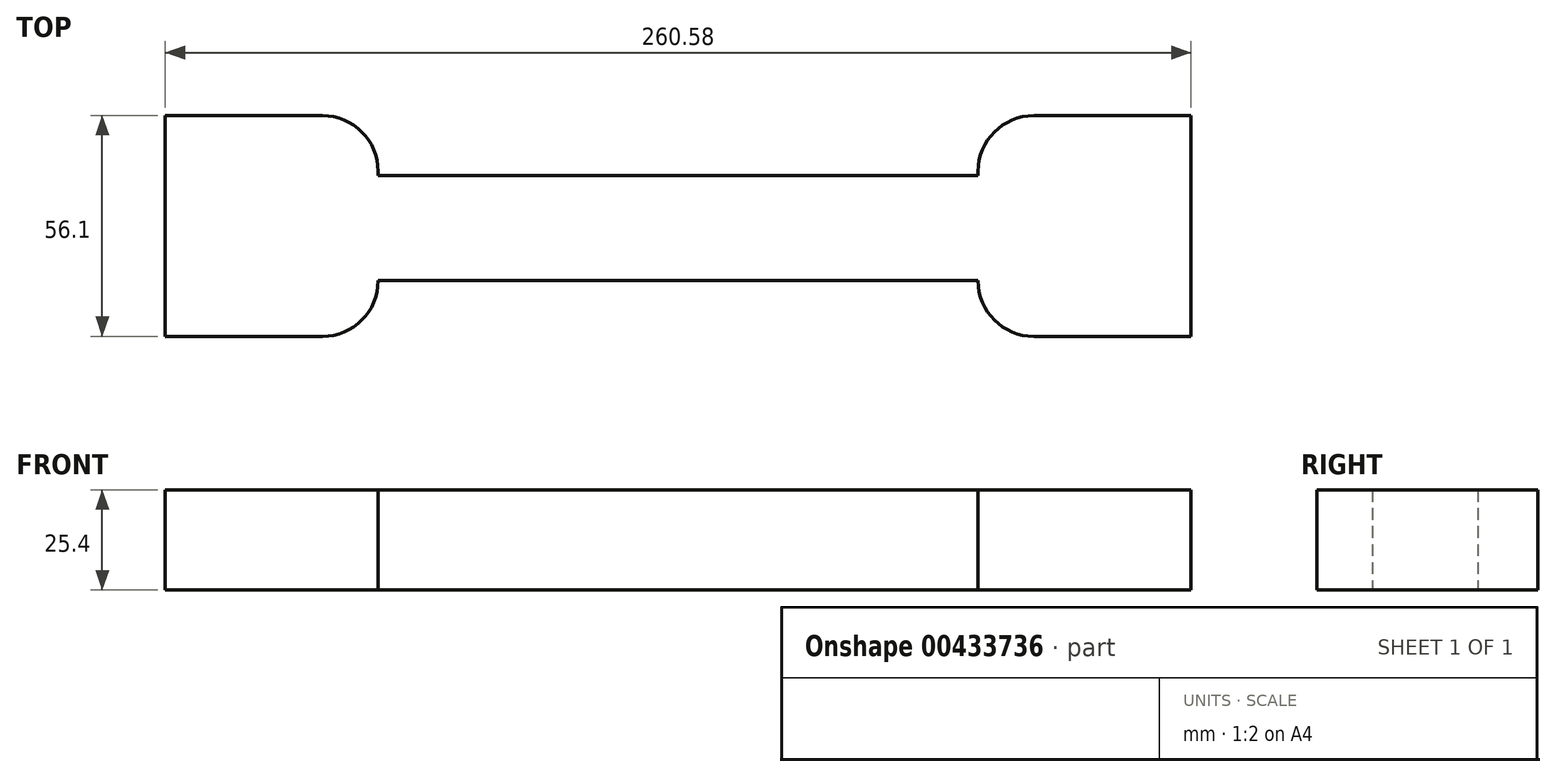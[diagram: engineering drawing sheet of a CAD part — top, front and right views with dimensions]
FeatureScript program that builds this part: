
annotation { "Feature Type Name" : "Feature", "Feature Type Description" : "" }
export const myFeature = defineFeature(function(context is Context, id is Id, definition is map)
    precondition{}
    {
        {
            var Q0;
            Q0=qCreatedBy(makeId("Top.planeOp"),FACE);
            var sketch = newSketch(context, id + "F0", { "sketchPlane" : qUnion([Q0])});
            skLineSegment(sketch, "E0.right", {"start": v(-76.21, 17.7) * mm, "end": v(-76.21, -14.48) * mm});
            skLineSegment(sketch, "E1.bottom", {"start": v(-90.36, 33.61) * mm, "end": v(-130.3, 33.61) * mm});
            skLineSegment(sketch, "E1.top", {"start": v(-90.36, -22.5) * mm, "end": v(-130.3, -22.5) * mm});
            skLineSegment(sketch, "E1.left", {"start": v(-76.21, 19.46) * mm, "end": v(-76.21, -8.35) * mm});
            skLineSegment(sketch, "E1.right", {"start": v(-130.3, 33.61) * mm, "end": v(-130.3, -22.5) * mm});
            skPoint(sketch, "E2.visualSharp", {"position": v(-76.21, 33.61) * mm});
            skArc(sketch, "E2.filletArc", {"start": v(-76.21, 19.46) * mm, "mid": v(-80.35, 29.47) * mm, "end": v(-90.36, 33.61) * mm});
            skPoint(sketch, "E3.visualSharp", {"position": v(-76.21, -22.5) * mm});
            skArc(sketch, "E3.filletArc", {"start": v(-90.36, -22.5) * mm, "mid": v(-80.35, -18.35) * mm, "end": v(-76.21, -8.35) * mm});
            skLineSegment(sketch, "E4.bottom", {"start": v(0, 18.34) * mm, "end": v(-76.21, 18.34) * mm});
            skLineSegment(sketch, "E4.top", {"start": v(0, -8.35) * mm, "end": v(-76.21, -8.35) * mm});
            skLineSegment(sketch, "E4.left", {"start": v(0, 18.34) * mm, "end": v(0, -8.35) * mm});
            skLineSegment(sketch, "E4.right", {"start": v(-76.21, 18.34) * mm, "end": v(-76.21, -8.35) * mm});
            skLineSegment(sketch, "E5.MirrorCS", {"start": v(0, -18.34) * mm, "end": v(0, 8.35) * mm});
            skLineSegment(sketch, "E6.MirrorCS", {"start": v(0, 18.34) * mm, "end": v(76.21, 18.34) * mm});
            skLineSegment(sketch, "E7.MirrorCS", {"start": v(0, -8.35) * mm, "end": v(76.21, -8.35) * mm});
            skArc(sketch, "E8.MirrorCS", {"start": v(76.21, 19.46) * mm, "mid": v(80.35, 29.47) * mm, "end": v(90.36, 33.61) * mm});
            skLineSegment(sketch, "E9.MirrorCS", {"start": v(90.36, 33.61) * mm, "end": v(130.3, 33.61) * mm});
            skLineSegment(sketch, "E10.MirrorCS", {"start": v(130.3, 33.61) * mm, "end": v(130.3, -22.5) * mm});
            skLineSegment(sketch, "E11.MirrorCS", {"start": v(90.36, -22.5) * mm, "end": v(130.3, -22.5) * mm});
            skArc(sketch, "E12.MirrorCS", {"start": v(90.36, -22.5) * mm, "mid": v(80.35, -18.35) * mm, "end": v(76.21, -8.35) * mm});
            skSolve(sketch);
        }
        {
            var Q0;
            {var subQ1=sQuery(id+"F0.wireOp",EDGE,"E4.bottom");Q0=makeQuery(id+"F0.imprint","IMPRINT",FACE,{"disambiguationData":[TD([[makeQuery(id+"F0.imprint","IMPRINT",EDGE,{"derivedFrom":subQ1}),1.0]])]});}
            var Q1;
            Q1=makeQuery(id+"F0.imprint","IMPRINT",FACE,{"disambiguationData":[TD([[makeQuery(id+"F0.imprint","IMPRINT",EDGE,{"derivedFrom":sQuery(id+"F0.wireOp",EDGE,"E1.bottom")}),1.0]])]});
            extrude(context, id + "F1", {"entities" : qUnion([Q0, Q1]), "depth" : 25.4 * mm});
        }
        {
            var Q0;
            Q0=makeQuery(id+"F1.opExtrude","SWEPT_BODY",BODY,{"disambiguationData":[OSD([sQuery(id+"F0.wireOp",EDGE,"E1.bottom"),sQuery(id+"F0.wireOp",EDGE,"E1.top"),sQuery(id+"F0.wireOp",EDGE,"E1.left"),sQuery(id+"F0.wireOp",EDGE,"E1.right"),sQuery(id+"F0.wireOp",EDGE,"E2.filletArc"),sQuery(id+"F0.wireOp",EDGE,"E3.filletArc"),sQuery(id+"F0.wireOp",EDGE,"E4.bottom"),sQuery(id+"F0.wireOp",EDGE,"E4.top"),sQuery(id+"F0.wireOp",EDGE,"E4.left"),sQuery(id+"F0.wireOp",EDGE,"E5.MirrorCS")])]});
            var Q1;
            Q1=makeQuery(id+"F1.opExtrude","SWEPT_FACE",FACE,{"disambiguationData":[OSD([sQuery(id+"F0.wireOp",EDGE,"E4.left"),sQuery(id+"F0.wireOp",EDGE,"E5.MirrorCS")])]});
            mirror(context, id + "F2", {"operationType" : NewBodyOperationType.ADD, "entities" : qUnion([Q0]), "mirrorPlane" : qUnion([Q1])});
        }
    });
